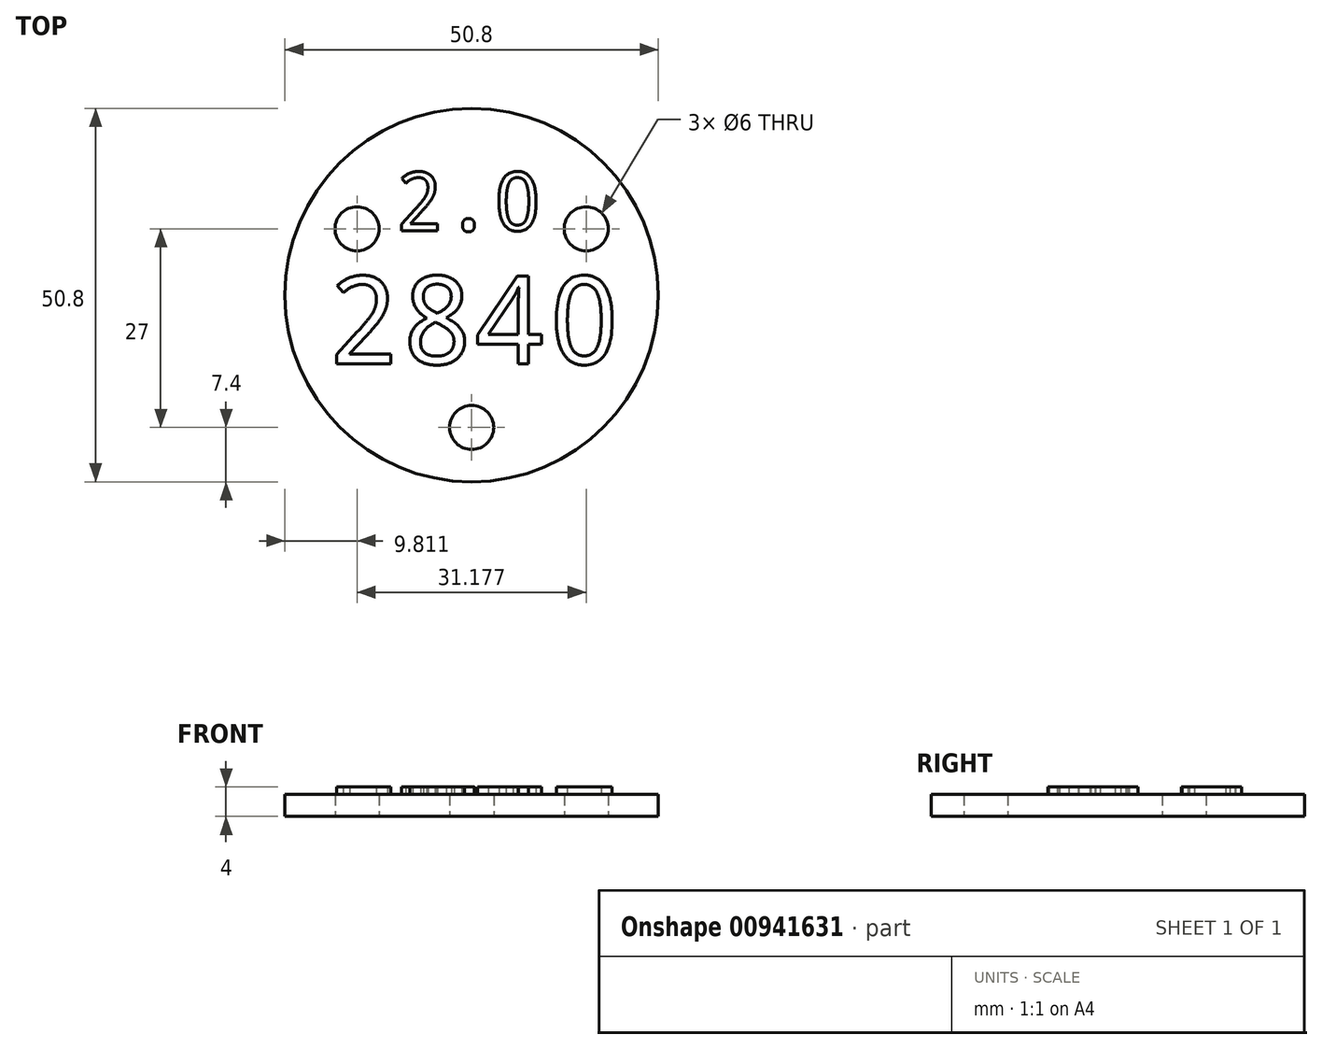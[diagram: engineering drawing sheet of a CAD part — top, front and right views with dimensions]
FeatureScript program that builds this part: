
annotation { "Feature Type Name" : "Feature", "Feature Type Description" : "" }
export const myFeature = defineFeature(function(context is Context, id is Id, definition is map)
    precondition{}
    {
        {
            var Q0;
            Q0=qCreatedBy(makeId("Top.planeOp"),FACE);
            var sketch = newSketch(context, id + "F0", { "sketchPlane" : qUnion([Q0])});
            skPoint(sketch, "E0", {"position": v(15.59, 9) * mm});
            skPoint(sketch, "E1.MirrorP", {"position": v(-15.59, 9) * mm});
            skPoint(sketch, "E2", {"position": v(0, -18) * mm});
            skCircle(sketch, "E3", {"center": v(0, 0) * mm, "radius": 25.4 * mm});
            skCircle(sketch, "E4", {"center": v(-15.59, 9) * mm, "radius": 3 * mm});
            skCircle(sketch, "E5", {"center": v(15.59, 9) * mm, "radius": 3 * mm});
            skCircle(sketch, "E6", {"center": v(0, -18) * mm, "radius": 3 * mm});
            skText(sketch, "E7", { "text": "2.0", "fontName": "DroidSansMono.ttf"});
            skText(sketch, "E8", { "text": "2840", "fontName": "DroidSansMono.ttf"});
            const initialGuessF0  = {"E7": [-0.01043, 0.00877, 1, 0, 0.008], "E8": [-0.01968, -0.00937, 1, 0, 0.012]};
            skSetInitialGuess(sketch, initialGuessF0);
            skSolve(sketch);
        }
        {
            var Q0;
            Q0=makeQuery(id+"F0.imprint","IMPRINT",FACE,{"disambiguationData":[TD([[makeQuery(id+"F0.imprint","IMPRINT",EDGE,{"derivedFrom":sQuery(id+"F0.wireOp",EDGE,"E8.sketch_text.stroke-18")}),-1.0]])]});
            var Q1;
            Q1=makeQuery(id+"F0.imprint","IMPRINT",FACE,{"disambiguationData":[TD([[makeQuery(id+"F0.imprint","IMPRINT",EDGE,{"derivedFrom":sQuery(id+"F0.wireOp",EDGE,"E8.sketch_text.stroke-37")}),1.0]])]});
            var Q2;
            Q2=makeQuery(id+"F0.imprint","IMPRINT",FACE,{"disambiguationData":[TD([[makeQuery(id+"F0.imprint","IMPRINT",EDGE,{"derivedFrom":sQuery(id+"F0.wireOp",EDGE,"E8.sketch_text.stroke-30")}),1.0]])]});
            var Q3;
            Q3=makeQuery(id+"F0.imprint","IMPRINT",FACE,{"disambiguationData":[TD([[makeQuery(id+"F0.imprint","IMPRINT",EDGE,{"derivedFrom":sQuery(id+"F0.wireOp",EDGE,"E8.sketch_text.stroke-55")}),1.0]])]});
            var Q4;
            Q4=makeQuery(id+"F0.imprint","IMPRINT",FACE,{"disambiguationData":[TD([[makeQuery(id+"F0.imprint","IMPRINT",EDGE,{"derivedFrom":sQuery(id+"F0.wireOp",EDGE,"E8.sketch_text.stroke-44")}),-1.0]])]});
            var Q5;
            Q5=makeQuery(id+"F0.imprint","IMPRINT",FACE,{"disambiguationData":[TD([[makeQuery(id+"F0.imprint","IMPRINT",EDGE,{"derivedFrom":sQuery(id+"F0.wireOp",EDGE,"E3")}),1.0]])]});
            var Q6;
            Q6=makeQuery(id+"F0.imprint","IMPRINT",FACE,{"disambiguationData":[TD([[makeQuery(id+"F0.imprint","IMPRINT",EDGE,{"derivedFrom":sQuery(id+"F0.wireOp",EDGE,"E8.sketch_text.stroke-61")}),-1.0]])]});
            var Q7;
            Q7=makeQuery(id+"F0.imprint","IMPRINT",FACE,{"disambiguationData":[TD([[makeQuery(id+"F0.imprint","IMPRINT",EDGE,{"derivedFrom":sQuery(id+"F0.wireOp",EDGE,"E8.sketch_text.stroke-67")}),1.0]])]});
            var Q8;
            Q8=makeQuery(id+"F0.imprint","IMPRINT",FACE,{"disambiguationData":[TD([[makeQuery(id+"F0.imprint","IMPRINT",EDGE,{"derivedFrom":sQuery(id+"F0.wireOp",EDGE,"E7.sketch_text.stroke-0")}),-1.0]])]});
            var Q9;
            Q9=makeQuery(id+"F0.imprint","IMPRINT",FACE,{"disambiguationData":[TD([[makeQuery(id+"F0.imprint","IMPRINT",EDGE,{"derivedFrom":sQuery(id+"F0.wireOp",EDGE,"E7.sketch_text.stroke-18")}),-1.0]])]});
            var Q10;
            Q10=makeQuery(id+"F0.imprint","IMPRINT",FACE,{"disambiguationData":[TD([[makeQuery(id+"F0.imprint","IMPRINT",EDGE,{"derivedFrom":sQuery(id+"F0.wireOp",EDGE,"E7.sketch_text.stroke-28")}),1.0]])]});
            var Q11;
            Q11=makeQuery(id+"F0.imprint","IMPRINT",FACE,{"disambiguationData":[TD([[makeQuery(id+"F0.imprint","IMPRINT",EDGE,{"derivedFrom":sQuery(id+"F0.wireOp",EDGE,"E7.sketch_text.stroke-22")}),-1.0]])]});
            var Q12;
            Q12=makeQuery(id+"F0.imprint","IMPRINT",FACE,{"disambiguationData":[TD([[makeQuery(id+"F0.imprint","IMPRINT",EDGE,{"derivedFrom":sQuery(id+"F0.wireOp",EDGE,"E8.sketch_text.stroke-0")}),-1.0]])]});
            extrude(context, id + "F1", {"entities" : qUnion([Q0, Q1, Q2, Q3, Q4, Q5, Q6, Q7, Q8, Q9, Q10, Q11, Q12]), "depth" : 3 * mm, "offsetDistance" : 25 * mm});
        }
        {
            var Q0;
            Q0=makeQuery(id+"F0.imprint","IMPRINT",FACE,{"disambiguationData":[TD([[makeQuery(id+"F0.imprint","IMPRINT",EDGE,{"derivedFrom":sQuery(id+"F0.wireOp",EDGE,"E7.sketch_text.stroke-0")}),-1.0]])]});
            var Q1;
            Q1=makeQuery(id+"F0.imprint","IMPRINT",FACE,{"disambiguationData":[TD([[makeQuery(id+"F0.imprint","IMPRINT",EDGE,{"derivedFrom":sQuery(id+"F0.wireOp",EDGE,"E7.sketch_text.stroke-18")}),-1.0]])]});
            var Q2;
            Q2=makeQuery(id+"F0.imprint","IMPRINT",FACE,{"disambiguationData":[TD([[makeQuery(id+"F0.imprint","IMPRINT",EDGE,{"derivedFrom":sQuery(id+"F0.wireOp",EDGE,"E7.sketch_text.stroke-22")}),-1.0]])]});
            var Q3;
            Q3=makeQuery(id+"F0.imprint","IMPRINT",FACE,{"disambiguationData":[TD([[makeQuery(id+"F0.imprint","IMPRINT",EDGE,{"derivedFrom":sQuery(id+"F0.wireOp",EDGE,"E8.sketch_text.stroke-0")}),-1.0]])]});
            var Q4;
            Q4=makeQuery(id+"F0.imprint","IMPRINT",FACE,{"disambiguationData":[TD([[makeQuery(id+"F0.imprint","IMPRINT",EDGE,{"derivedFrom":sQuery(id+"F0.wireOp",EDGE,"E8.sketch_text.stroke-18")}),-1.0]])]});
            var Q5;
            Q5=makeQuery(id+"F0.imprint","IMPRINT",FACE,{"disambiguationData":[TD([[makeQuery(id+"F0.imprint","IMPRINT",EDGE,{"derivedFrom":sQuery(id+"F0.wireOp",EDGE,"E8.sketch_text.stroke-44")}),-1.0]])]});
            var Q6;
            Q6=makeQuery(id+"F0.imprint","IMPRINT",FACE,{"disambiguationData":[TD([[makeQuery(id+"F0.imprint","IMPRINT",EDGE,{"derivedFrom":sQuery(id+"F0.wireOp",EDGE,"E8.sketch_text.stroke-61")}),-1.0]])]});
            extrude(context, id + "F2", {"entities" : qUnion([Q0, Q1, Q2, Q3, Q4, Q5, Q6]), "operationType" : NewBodyOperationType.ADD, "depth" : 4 * mm, "offsetDistance" : 25 * mm});
        }
    });
